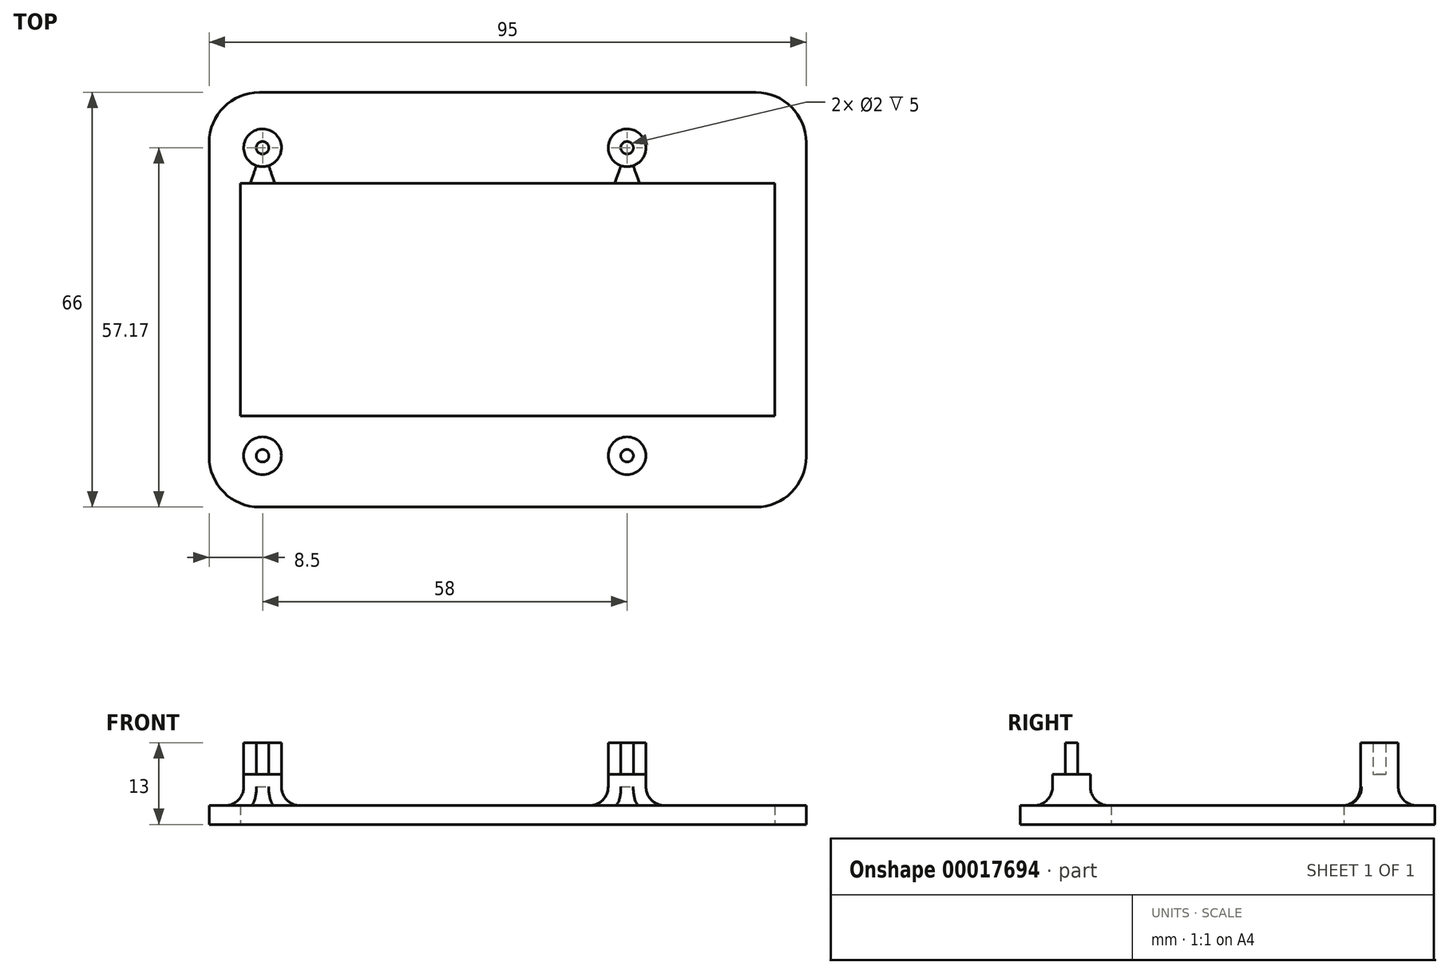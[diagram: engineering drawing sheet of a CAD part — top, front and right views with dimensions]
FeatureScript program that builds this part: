
annotation { "Feature Type Name" : "Feature", "Feature Type Description" : "" }
export const myFeature = defineFeature(function(context is Context, id is Id, definition is map)
    precondition{}
    {
        {
            var Q0;
            Q0=qCreatedBy(makeId("Top.planeOp"),FACE);
            var sketch = newSketch(context, id + "F0", { "sketchPlane" : qUnion([Q0])});
            skCircle(sketch, "E0", {"center": v(3.5, 3.5) * mm, "radius": 1 * mm});
            skCircle(sketch, "E1", {"center": v(61.5, 3.5) * mm, "radius": 1 * mm});
            skCircle(sketch, "E2.MirrorC", {"center": v(3.5, 52.5) * mm, "radius": 1 * mm});
            skCircle(sketch, "E3.MirrorC", {"center": v(61.5, 52.5) * mm, "radius": 1 * mm});
            skLineSegment(sketch, "E4.0", {"start": v(-5, 61.33) * mm, "end": v(90, 61.33) * mm});
            skLineSegment(sketch, "E4.1", {"start": v(-5, -4.67) * mm, "end": v(-5, 61.33) * mm});
            skLineSegment(sketch, "E4.2", {"start": v(-5, -4.67) * mm, "end": v(90, -4.67) * mm});
            skLineSegment(sketch, "E4.3", {"start": v(90, -4.67) * mm, "end": v(90, 61.33) * mm});
            skCircle(sketch, "E5.0", {"center": v(61.5, 52.5) * mm, "radius": 3 * mm});
            skCircle(sketch, "E6.0", {"center": v(3.5, 52.5) * mm, "radius": 3 * mm});
            skCircle(sketch, "E7.0", {"center": v(3.5, 3.5) * mm, "radius": 3 * mm});
            skCircle(sketch, "E8.0", {"center": v(61.5, 3.5) * mm, "radius": 3 * mm});
            skLineSegment(sketch, "E9", {"start": v(-5, 28.33) * mm, "end": v(90, 28.33) * mm});
            skLineSegment(sketch, "E10.rect.bottom", {"start": v(0, 9.83) * mm, "end": v(85, 9.83) * mm});
            skLineSegment(sketch, "E10.rect.top", {"start": v(0, 46.83) * mm, "end": v(85, 46.83) * mm});
            skLineSegment(sketch, "E10.rect.left", {"start": v(0, 9.83) * mm, "end": v(0, 46.83) * mm});
            skLineSegment(sketch, "E10.rect.right", {"start": v(85, 9.83) * mm, "end": v(85, 46.83) * mm});
            skPoint(sketch, "E10.rect.middle", {"position": v(42.5, 28.33) * mm});
            skSolve(sketch);
        }
        {
            var Q0;
            {var subQ10=sQuery(id+"F0.wireOp",EDGE,"E4.0");Q0=makeQuery(id+"F0.imprint","IMPRINT",FACE,{"disambiguationData":[TD([[makeQuery(id+"F0.imprint","IMPRINT",EDGE,{"derivedFrom":subQ10}),-1.0]])]});}
            var Q1;
            {var subQ10=sQuery(id+"F0.wireOp",EDGE,"E4.2");Q1=makeQuery(id+"F0.imprint","IMPRINT",FACE,{"disambiguationData":[TD([[makeQuery(id+"F0.imprint","IMPRINT",EDGE,{"derivedFrom":subQ10}),1.0]])]});}
            var Q2;
            Q2=makeQuery(id+"F0.imprint","IMPRINT",FACE,{"disambiguationData":[TD([[makeQuery(id+"F0.imprint","IMPRINT",EDGE,{"derivedFrom":sQuery(id+"F0.wireOp",EDGE,"E0")}),-1.0]])]});
            var Q3;
            Q3=makeQuery(id+"F0.imprint","IMPRINT",FACE,{"disambiguationData":[TD([[makeQuery(id+"F0.imprint","IMPRINT",EDGE,{"derivedFrom":sQuery(id+"F0.wireOp",EDGE,"E0")}),1.0]])]});
            var Q4;
            Q4=makeQuery(id+"F0.imprint","IMPRINT",FACE,{"disambiguationData":[TD([[makeQuery(id+"F0.imprint","IMPRINT",EDGE,{"derivedFrom":sQuery(id+"F0.wireOp",EDGE,"E1")}),-1.0]])]});
            var Q5;
            Q5=makeQuery(id+"F0.imprint","IMPRINT",FACE,{"disambiguationData":[TD([[makeQuery(id+"F0.imprint","IMPRINT",EDGE,{"derivedFrom":sQuery(id+"F0.wireOp",EDGE,"E1")}),1.0]])]});
            var Q6;
            Q6=makeQuery(id+"F0.imprint","IMPRINT",FACE,{"disambiguationData":[TD([[makeQuery(id+"F0.imprint","IMPRINT",EDGE,{"derivedFrom":sQuery(id+"F0.wireOp",EDGE,"E3.MirrorC")}),1.0]])]});
            var Q7;
            Q7=makeQuery(id+"F0.imprint","IMPRINT",FACE,{"disambiguationData":[TD([[makeQuery(id+"F0.imprint","IMPRINT",EDGE,{"derivedFrom":sQuery(id+"F0.wireOp",EDGE,"E3.MirrorC")}),-1.0]])]});
            var Q8;
            Q8=makeQuery(id+"F0.imprint","IMPRINT",FACE,{"disambiguationData":[TD([[makeQuery(id+"F0.imprint","IMPRINT",EDGE,{"derivedFrom":sQuery(id+"F0.wireOp",EDGE,"E2.MirrorC")}),1.0]])]});
            var Q9;
            Q9=makeQuery(id+"F0.imprint","IMPRINT",FACE,{"disambiguationData":[TD([[makeQuery(id+"F0.imprint","IMPRINT",EDGE,{"derivedFrom":sQuery(id+"F0.wireOp",EDGE,"E2.MirrorC")}),-1.0]])]});
            extrude(context, id + "F1", {"entities" : qUnion([Q0, Q1, Q2, Q3, Q4, Q5, Q6, Q7, Q8, Q9]), "depth" : 3 * mm});
        }
        {
            var Q0;
            Q0=makeQuery(id+"F0.imprint","IMPRINT",FACE,{"disambiguationData":[TD([[makeQuery(id+"F0.imprint","IMPRINT",EDGE,{"derivedFrom":sQuery(id+"F0.wireOp",EDGE,"E2.MirrorC")}),1.0]])]});
            var Q1;
            Q1=makeQuery(id+"F0.imprint","IMPRINT",FACE,{"disambiguationData":[TD([[makeQuery(id+"F0.imprint","IMPRINT",EDGE,{"derivedFrom":sQuery(id+"F0.wireOp",EDGE,"E2.MirrorC")}),-1.0]])]});
            var Q2;
            Q2=makeQuery(id+"F0.imprint","IMPRINT",FACE,{"disambiguationData":[TD([[makeQuery(id+"F0.imprint","IMPRINT",EDGE,{"derivedFrom":sQuery(id+"F0.wireOp",EDGE,"E0")}),1.0]])]});
            var Q3;
            Q3=makeQuery(id+"F0.imprint","IMPRINT",FACE,{"disambiguationData":[TD([[makeQuery(id+"F0.imprint","IMPRINT",EDGE,{"derivedFrom":sQuery(id+"F0.wireOp",EDGE,"E0")}),-1.0]])]});
            var Q4;
            Q4=makeQuery(id+"F0.imprint","IMPRINT",FACE,{"disambiguationData":[TD([[makeQuery(id+"F0.imprint","IMPRINT",EDGE,{"derivedFrom":sQuery(id+"F0.wireOp",EDGE,"E1")}),-1.0]])]});
            var Q5;
            Q5=makeQuery(id+"F0.imprint","IMPRINT",FACE,{"disambiguationData":[TD([[makeQuery(id+"F0.imprint","IMPRINT",EDGE,{"derivedFrom":sQuery(id+"F0.wireOp",EDGE,"E1")}),1.0]])]});
            var Q6;
            Q6=makeQuery(id+"F0.imprint","IMPRINT",FACE,{"disambiguationData":[TD([[makeQuery(id+"F0.imprint","IMPRINT",EDGE,{"derivedFrom":sQuery(id+"F0.wireOp",EDGE,"E3.MirrorC")}),-1.0]])]});
            var Q7;
            Q7=makeQuery(id+"F0.imprint","IMPRINT",FACE,{"disambiguationData":[TD([[makeQuery(id+"F0.imprint","IMPRINT",EDGE,{"derivedFrom":sQuery(id+"F0.wireOp",EDGE,"E3.MirrorC")}),1.0]])]});
            extrude(context, id + "F2", {"entities" : qUnion([Q0, Q1, Q2, Q3, Q4, Q5, Q6, Q7]), "operationType" : NewBodyOperationType.ADD, "depth" : 8 * mm});
        }
        {
            var Q0;
            Q0=makeQuery(id+"F0.imprint","IMPRINT",FACE,{"disambiguationData":[TD([[makeQuery(id+"F0.imprint","IMPRINT",EDGE,{"derivedFrom":sQuery(id+"F0.wireOp",EDGE,"E1")}),1.0]])]});
            var Q1;
            Q1=makeQuery(id+"F0.imprint","IMPRINT",FACE,{"disambiguationData":[TD([[makeQuery(id+"F0.imprint","IMPRINT",EDGE,{"derivedFrom":sQuery(id+"F0.wireOp",EDGE,"E0")}),1.0]])]});
            var Q2;
            Q2=makeQuery(id+"F0.imprint","IMPRINT",FACE,{"disambiguationData":[TD([[makeQuery(id+"F0.imprint","IMPRINT",EDGE,{"derivedFrom":sQuery(id+"F0.wireOp",EDGE,"E2.MirrorC")}),-1.0]])]});
            var Q3;
            Q3=makeQuery(id+"F0.imprint","IMPRINT",FACE,{"disambiguationData":[TD([[makeQuery(id+"F0.imprint","IMPRINT",EDGE,{"derivedFrom":sQuery(id+"F0.wireOp",EDGE,"E3.MirrorC")}),-1.0]])]});
            extrude(context, id + "F3", {"entities" : qUnion([Q0, Q1, Q2, Q3]), "operationType" : NewBodyOperationType.ADD, "depth" : 13 * mm});
        }
        {
            var Q0;
            Q0=makeQuery(id+"F1.opExtrude","SWEPT_EDGE",EDGE,{"disambiguationData":[OSD([sQuery(id+"F0.wireOp",EDGE,"E4.0"),sQuery(id+"F0.wireOp",EDGE,"E4.3")])]});
            var Q1;
            Q1=makeQuery(id+"F1.opExtrude","SWEPT_EDGE",EDGE,{"disambiguationData":[OSD([sQuery(id+"F0.wireOp",EDGE,"E4.2"),sQuery(id+"F0.wireOp",EDGE,"E4.3")])]});
            var Q2;
            Q2=makeQuery(id+"F1.opExtrude","SWEPT_EDGE",EDGE,{"disambiguationData":[OSD([sQuery(id+"F0.wireOp",EDGE,"E4.1"),sQuery(id+"F0.wireOp",EDGE,"E4.2")])]});
            var Q3;
            Q3=makeQuery(id+"F1.opExtrude","SWEPT_EDGE",EDGE,{"disambiguationData":[OSD([sQuery(id+"F0.wireOp",EDGE,"E4.0"),sQuery(id+"F0.wireOp",EDGE,"E4.1")])]});
            fillet(context, id + "F4", {"entities" : qUnion([Q0, Q1, Q2, Q3]), "radius" : 8 * mm, "tangentPropagation" : true, "allowEdgeOverflow" : false});
        }
        {
            var Q0;
            Q0=makeQuery(id+"F2.boolean.opBoolean","INTERSECT",EDGE,{"derivedFrom":[makeQuery(id+"F1.opExtrude","CAP_FACE",FACE,{"disambiguationData":[OSD([sQuery(id+"F0.wireOp",EDGE,"E4.0"),sQuery(id+"F0.wireOp",EDGE,"E4.1"),sQuery(id+"F0.wireOp",EDGE,"E4.2"),sQuery(id+"F0.wireOp",EDGE,"E4.3"),sQuery(id+"F0.wireOp",EDGE,"E10.rect.bottom"),sQuery(id+"F0.wireOp",EDGE,"E10.rect.top"),sQuery(id+"F0.wireOp",EDGE,"E10.rect.left"),sQuery(id+"F0.wireOp",EDGE,"E10.rect.right")])],"isStart":false}),makeQuery(id+"F2.opExtrude","SWEPT_FACE",FACE,{"disambiguationData":[OSD([sQuery(id+"F0.wireOp",EDGE,"E6.0")])]})]});
            var Q1;
            Q1=makeQuery(id+"F2.boolean.opBoolean","INTERSECT",EDGE,{"derivedFrom":[makeQuery(id+"F1.opExtrude","CAP_FACE",FACE,{"disambiguationData":[OSD([sQuery(id+"F0.wireOp",EDGE,"E4.0"),sQuery(id+"F0.wireOp",EDGE,"E4.1"),sQuery(id+"F0.wireOp",EDGE,"E4.2"),sQuery(id+"F0.wireOp",EDGE,"E4.3"),sQuery(id+"F0.wireOp",EDGE,"E10.rect.bottom"),sQuery(id+"F0.wireOp",EDGE,"E10.rect.top"),sQuery(id+"F0.wireOp",EDGE,"E10.rect.left"),sQuery(id+"F0.wireOp",EDGE,"E10.rect.right")])],"isStart":false}),makeQuery(id+"F2.opExtrude","SWEPT_FACE",FACE,{"disambiguationData":[OSD([sQuery(id+"F0.wireOp",EDGE,"E7.0")])]})]});
            var Q2;
            Q2=makeQuery(id+"F2.boolean.opBoolean","INTERSECT",EDGE,{"derivedFrom":[makeQuery(id+"F1.opExtrude","CAP_FACE",FACE,{"disambiguationData":[OSD([sQuery(id+"F0.wireOp",EDGE,"E4.0"),sQuery(id+"F0.wireOp",EDGE,"E4.1"),sQuery(id+"F0.wireOp",EDGE,"E4.2"),sQuery(id+"F0.wireOp",EDGE,"E4.3"),sQuery(id+"F0.wireOp",EDGE,"E10.rect.bottom"),sQuery(id+"F0.wireOp",EDGE,"E10.rect.top"),sQuery(id+"F0.wireOp",EDGE,"E10.rect.left"),sQuery(id+"F0.wireOp",EDGE,"E10.rect.right")])],"isStart":false}),makeQuery(id+"F2.opExtrude","SWEPT_FACE",FACE,{"disambiguationData":[OSD([sQuery(id+"F0.wireOp",EDGE,"E8.0")])]})]});
            var Q3;
            Q3=makeQuery(id+"F2.boolean.opBoolean","INTERSECT",EDGE,{"derivedFrom":[makeQuery(id+"F1.opExtrude","CAP_FACE",FACE,{"disambiguationData":[OSD([sQuery(id+"F0.wireOp",EDGE,"E4.0"),sQuery(id+"F0.wireOp",EDGE,"E4.1"),sQuery(id+"F0.wireOp",EDGE,"E4.2"),sQuery(id+"F0.wireOp",EDGE,"E4.3"),sQuery(id+"F0.wireOp",EDGE,"E10.rect.bottom"),sQuery(id+"F0.wireOp",EDGE,"E10.rect.top"),sQuery(id+"F0.wireOp",EDGE,"E10.rect.left"),sQuery(id+"F0.wireOp",EDGE,"E10.rect.right")])],"isStart":false}),makeQuery(id+"F2.opExtrude","SWEPT_FACE",FACE,{"disambiguationData":[OSD([sQuery(id+"F0.wireOp",EDGE,"E5.0")])]})]});
            fillet(context, id + "F5", {"entities" : qUnion([Q0, Q1, Q2, Q3]), "radius" : 3 * mm, "tangentPropagation" : true, "allowEdgeOverflow" : false});
        }
    });
